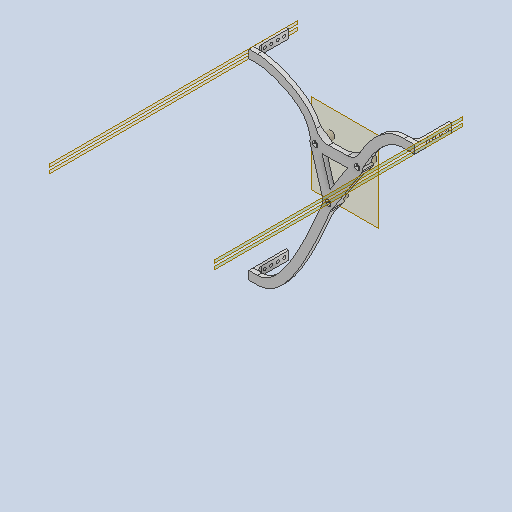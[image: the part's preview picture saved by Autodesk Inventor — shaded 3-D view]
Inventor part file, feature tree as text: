
AUTODESK INVENTOR PART (.ipt)
format: ipt  version: 2024.2 (Build 282272000, 272)  size: 524,288 bytes
history: native  units: mm
features: other x27, sketch x7, extrude x7, projected_geometry x5, fillet x3
ambient origin geometry x8: Origin, YZ Plane, XZ Plane, XY Plane, X Axis, Y Axis, Z Axis, Center Point
bodies: Solide1 (feature_tree)
feature tree (49):
  other  "Plan de construction1"
  sketch  "Esquisse1"
  other  "Plan de construction2"
  extrude  "Extrusion1"  Depth=2.5mm
  extrude  "Extrusion2"  Depth=2.5mm
  extrude  "Extrusion3"  Depth=2.5mm
  extrude  "Extrusion4"  Depth=10.0mm TaperAngle=0.0deg
  extrude  "Extrusion5"  Depth=5.0mm TaperAngle=0.0deg
  fillet  "Congé1"  Radius=12.0mm
  fillet  "Congé2"  Radius=12.0mm
  other  "Plan de construction3"
  other  "Plan de construction4"
  other  "Plan de construction5"
  extrude  "Extrusion8"  Depth=12.0mm
  other  "Plan de construction6"
  extrude  "Extrusion9"  Depth=5.0mm TaperAngle=0.0deg
  fillet  "Congé4"  Radius=5.8mm
  other  "Référence1"
  other  "Référence2"
  other  "Référence3"
  sketch  "Esquisse3"
  projected_geometry  "Boucle projetée1"
  projected_geometry  "Boucle projetée2"
  projected_geometry  "Boucle projetée3"
  sketch  "Esquisse4"
  projected_geometry  "Boucle projetée4"
  sketch  "Esquisse5"
  sketch  "Esquisse7"
  projected_geometry  "Boucle projetée6"
  other  "Référence4"
  other  "Référence5"
  other  "Référence6"
  sketch  "Esquisse10"
  other  "Référence9"
  other  "Référence10"
  sketch  "Esquisse11"
  other  "<userpath>\Desktop\meca_robotbebou\iks01A2\iks01A2.iam"
  other  "iks01A2.iam"
  other  "NUCLEO-F411RE:1"
  other  "<userpath>\Desktop\meca_robotbebou\Robotbebou.iam"
  other  "Robotbebou.iam"
  other  "MakerBeam-cube:1"
  other  "MakerBeam-cube_MIR1:1"
  other  "MakerBeam-cube_MIR_MIR:1"
  other  "MakerBeam-cube_MIR_MIR1_MIR:1"
  other  "MakerBeam-cube_MIR_MIR2:1"
  other  "<userpath>\Desktop\export\Robotbebou.iam"
  other  "profile259_MIR_MIR:1"
  other  "profile259_MIR:1"
